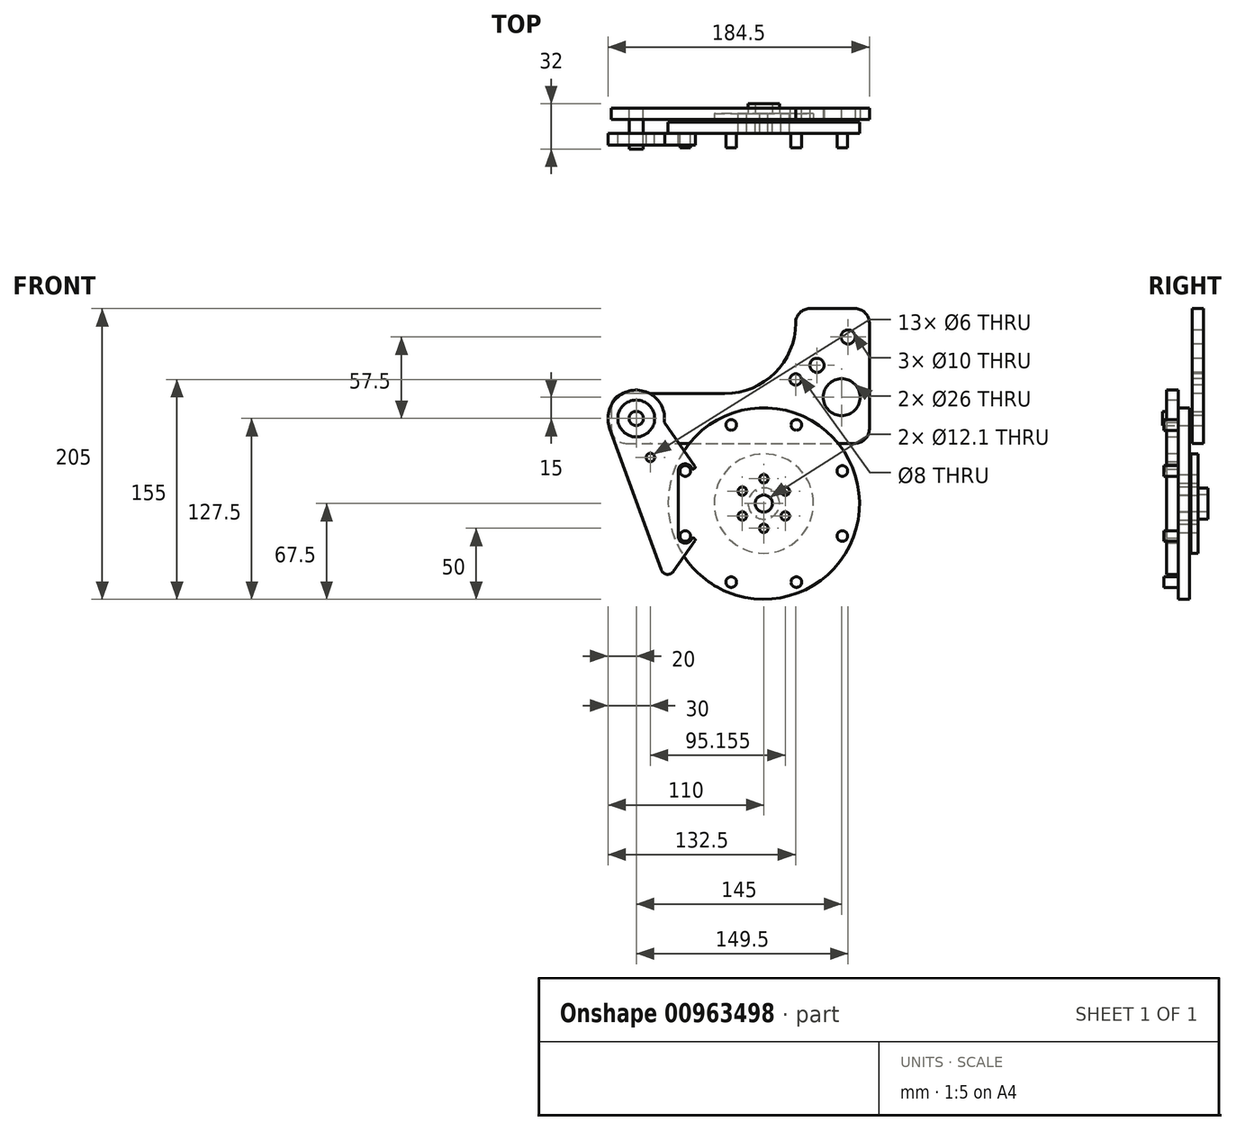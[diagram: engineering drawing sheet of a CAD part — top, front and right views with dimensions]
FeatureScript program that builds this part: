
annotation { "Feature Type Name" : "Feature", "Feature Type Description" : "" }
export const myFeature = defineFeature(function(context is Context, id is Id, definition is map)
    precondition{}
    {
        {
            var Q0;
            Q0=qCreatedBy(makeId("Front.planeOp"),FACE);
            var sketch = newSketch(context, id + "F0", { "sketchPlane" : qUnion([Q0])});
            skCircle(sketch, "E0", {"center": v(0, 0) * mm, "radius": 67.5 * mm});
            skCircle(sketch, "E1", {"center": v(0, 0) * mm, "radius": 6.05 * mm});
            skSolve(sketch);
        }
        {
            var Q0;
            Q0=qSketchRegion(id+"F0",true);
            extrude(context, id + "F1", {"entities" : qUnion([Q0]), "depth" : 5 * mm, "hasSecondDirection" : true, "secondDirectionOppositeDirection" : true, "secondDirectionDepth" : 3 * mm});
        }
        {
            var Q0;
            Q0=makeQuery(id+"F1.opExtrude","CAP_FACE",FACE,{"disambiguationData":[OSD([sQuery(id+"F0.wireOp",EDGE,"E0"),sQuery(id+"F0.wireOp",EDGE,"E1")])],"isStart":false});
            var sketch = newSketch(context, id + "F2", { "sketchPlane" : qUnion([Q0])});
            skCircle(sketch, "E2", {"center": v(0, 0) * mm, "radius": 60 * mm, "construction": true});
            skCircle(sketch, "E3", {"center": v(0, 60) * mm, "radius": 3.75 * mm});
            skCircle(sketch, "E4.1.0", {"center": v(-42.43, 42.43) * mm, "radius": 3.75 * mm});
            skCircle(sketch, "E4.2.0", {"center": v(-60, 0) * mm, "radius": 3.75 * mm});
            skCircle(sketch, "E4.3.0", {"center": v(-42.43, -42.43) * mm, "radius": 3.75 * mm});
            skCircle(sketch, "E4.4.0", {"center": v(0, -60) * mm, "radius": 3.75 * mm});
            skCircle(sketch, "E4.5.0", {"center": v(42.43, -42.43) * mm, "radius": 3.75 * mm});
            skCircle(sketch, "E4.6.0", {"center": v(60, 0) * mm, "radius": 3.75 * mm});
            skCircle(sketch, "E4.7.0", {"center": v(42.43, 42.43) * mm, "radius": 3.75 * mm});
            skPoint(sketch, "E5", {"position": v(0, -77) * mm});
            skSolve(sketch);
        }
        {
            var Q0;
            Q0=qSketchRegion(id+"F2",true);
            extrude(context, id + "F3", {"entities" : qUnion([Q0]), "operationType" : NewBodyOperationType.ADD, "depth" : 10 * mm});
        }
        {
            var Q0;
            Q0=qCreatedBy(makeId("Right.planeOp"),FACE);
            var sketch = newSketch(context, id + "F4", { "sketchPlane" : qUnion([Q0])});
            skLineSegment(sketch, "E6", {"start": v(-64.67, -77) * mm, "end": v(70.6, -77) * mm});
            skLineSegment(sketch, "E7", {"start": v(-72, 0) * mm, "end": v(117.3, 0) * mm});
            skLineSegment(sketch, "E8", {"start": v(-81.45, 67) * mm, "end": v(84.45, 67) * mm});
            skSolve(sketch);
        }
        {
            var Q0;
            Q0=makeQuery(id+"F1.opExtrude","CAP_FACE",FACE,{"disambiguationData":[OSD([sQuery(id+"F0.wireOp",EDGE,"E0"),sQuery(id+"F0.wireOp",EDGE,"E1")])],"isStart":false});
            var sketch = newSketch(context, id + "F5", { "sketchPlane" : qUnion([Q0])});
            skLineSegment(sketch, "E9", {"start": v(22.5, 127.5) * mm, "end": v(22.5, 127.5) * mm});
            skLineSegment(sketch, "E10", {"start": v(-27.5, 77.5) * mm, "end": v(-97.5, 77.5) * mm});
            skLineSegment(sketch, "E11", {"start": v(-107.5, 67.5) * mm, "end": v(-107.5, 52.5) * mm});
            skLineSegment(sketch, "E12", {"start": v(-97.5, 42.5) * mm, "end": v(-75.62, 42.5) * mm});
            skLineSegment(sketch, "E13", {"start": v(64.5, 137.5) * mm, "end": v(32.5, 137.5) * mm});
            skCircle(sketch, "E14", {"center": v(55, 75) * mm, "radius": 13 * mm});
            skCircle(sketch, "E15", {"center": v(-90, 60) * mm, "radius": 5 * mm});
            skCircle(sketch, "E16", {"center": v(59.5, 117.5) * mm, "radius": 5 * mm});
            skCircle(sketch, "E17", {"center": v(37.5, 97.5) * mm, "radius": 5 * mm});
            skPoint(sketch, "E18.visualSharp", {"position": v(-107.5, 77.5) * mm});
            skArc(sketch, "E18.filletArc", {"start": v(-97.5, 77.5) * mm, "mid": v(-104.57, 74.57) * mm, "end": v(-107.5, 67.5) * mm});
            skPoint(sketch, "E19.visualSharp", {"position": v(-107.5, 42.5) * mm});
            skArc(sketch, "E19.filletArc", {"start": v(-107.5, 52.5) * mm, "mid": v(-104.57, 45.43) * mm, "end": v(-97.5, 42.5) * mm});
            skArc(sketch, "E20.filletArc", {"start": v(-27.5, 77.5) * mm, "mid": v(7.86, 92.14) * mm, "end": v(22.5, 127.5) * mm});
            skArc(sketch, "E21.filletArc", {"start": v(32.5, 137.5) * mm, "mid": v(25.43, 134.57) * mm, "end": v(22.5, 127.5) * mm});
            skLineSegment(sketch, "E22", {"start": v(74.5, 127.5) * mm, "end": v(74.5, 52.5) * mm});
            skPoint(sketch, "E23.visualSharp", {"position": v(74.5, 137.5) * mm});
            skArc(sketch, "E23.filletArc", {"start": v(74.5, 127.5) * mm, "mid": v(71.57, 134.57) * mm, "end": v(64.5, 137.5) * mm});
            skPoint(sketch, "E24.visualSharp", {"position": v(74.5, 42.5) * mm});
            skArc(sketch, "E24.filletArc", {"start": v(64.5, 42.5) * mm, "mid": v(71.57, 45.43) * mm, "end": v(74.5, 52.5) * mm});
            skLineSegment(sketch, "E25.trimOffspring", {"start": v(-75.62, 42.5) * mm, "end": v(64.5, 42.5) * mm});
            skCircle(sketch, "E26", {"center": v(22.5, 87.5) * mm, "radius": 4 * mm});
            skSolve(sketch);
        }
        {
            var Q0;
            Q0=makeQuery(id+"F1.opExtrude","SWEPT_BODY",BODY,{"disambiguationData":[OSD([sQuery(id+"F0.wireOp",EDGE,"E0"),sQuery(id+"F0.wireOp",EDGE,"E1")])]});
            var Q1;
            Q1=sQuery(id+"F4.wireOp",EDGE,"E7");
            transform(context, id + "F6", {"entities" : qUnion([Q0]), "transformType" : TransformType.ROTATION, "transformAxis" : qUnion([Q1]), "angle" : 22.5 * degree, "makeCopy" : false});
        }
        {
            var Q0;
            Q0=qSketchRegion(id+"F5",true);
            extrude(context, id + "F7", {"entities" : qUnion([Q0]), "oppositeDirection" : true, "depth" : 8 * mm});
        }
        {
            var Q0;
            Q0=makeQuery(id+"F7.opExtrude","SWEPT_BODY",BODY,{"disambiguationData":[OSD([sQuery(id+"F5.wireOp",EDGE,"E9"),sQuery(id+"F5.wireOp",EDGE,"E10"),sQuery(id+"F5.wireOp",EDGE,"E11"),sQuery(id+"F5.wireOp",EDGE,"E12"),sQuery(id+"F5.wireOp",EDGE,"E13"),sQuery(id+"F5.wireOp",EDGE,"E14"),sQuery(id+"F5.wireOp",EDGE,"E15"),sQuery(id+"F5.wireOp",EDGE,"E16"),sQuery(id+"F5.wireOp",EDGE,"E17"),sQuery(id+"F5.wireOp",EDGE,"E18.filletArc"),sQuery(id+"F5.wireOp",EDGE,"E19.filletArc"),sQuery(id+"F5.wireOp",EDGE,"E20.filletArc"),sQuery(id+"F5.wireOp",EDGE,"E21.filletArc"),sQuery(id+"F5.wireOp",EDGE,"E22"),sQuery(id+"F5.wireOp",EDGE,"E23.filletArc"),sQuery(id+"F5.wireOp",EDGE,"E24.filletArc"),sQuery(id+"F5.wireOp",EDGE,"E25.trimOffspring")])]});
            transform(context, id + "F8", {"entities" : qUnion([Q0]), "transformType" : TransformType.TRANSLATION_3D, "dx" : 0 * mm, "dy" : 10 * mm, "dz" : 0 * mm, "makeCopy" : false});
        }
        {
            var Q0;
            Q0=makeQuery(id+"F1.opExtrude","CAP_FACE",FACE,{"disambiguationData":[OSD([sQuery(id+"F0.wireOp",EDGE,"E0"),sQuery(id+"F0.wireOp",EDGE,"E1")])],"isStart":false});
            var sketch = newSketch(context, id + "F9", { "sketchPlane" : qUnion([Q0])});
            skCircle(sketch, "E27", {"center": v(-90, 60) * mm, "radius": 13 * mm});
            skArc(sketch, "E28", {"start": v(-70.2, 57.14) * mm, "mid": v(-92.05, 79.9) * mm, "end": v(-108.8, 53.16) * mm});
            skLineSegment(sketch, "E29", {"start": v(-48.55, -26.21) * mm, "end": v(-63.67, -47.8) * mm});
            skLineSegment(sketch, "E30", {"start": v(-72.47, -46.65) * mm, "end": v(-108.8, 53.16) * mm});
            skPoint(sketch, "E31.visualSharp", {"position": v(-69.18, -55.67) * mm});
            skArc(sketch, "E31.filletArc", {"start": v(-72.47, -46.65) * mm, "mid": v(-68.42, -49.9) * mm, "end": v(-63.67, -47.8) * mm});
            skCircle(sketch, "E32", {"center": v(-80, 32.5) * mm, "radius": 3 * mm});
            skArc(sketch, "E33", {"start": v(-60.43, -22.96) * mm, "mid": v(-56.44, -27.86) * mm, "end": v(-50.84, -24.93) * mm});
            skLineSegment(sketch, "E34", {"start": v(-48.87, -24.77) * mm, "end": v(-49.42, -24.46) * mm});
            skPoint(sketch, "E35.visualSharp", {"position": v(-47.93, -25.32) * mm});
            skArc(sketch, "E35.filletArc", {"start": v(-48.55, -26.21) * mm, "mid": v(-48.4, -25.42) * mm, "end": v(-48.87, -24.77) * mm});
            skArc(sketch, "E36", {"start": v(-50.84, 24.93) * mm, "mid": v(-56.44, 27.86) * mm, "end": v(-60.43, 22.96) * mm});
            skLineSegment(sketch, "E37", {"start": v(-60.43, 22.96) * mm, "end": v(-60.43, -22.96) * mm});
            skLineSegment(sketch, "E38", {"start": v(-70.2, 57.14) * mm, "end": v(-48.55, 26.21) * mm});
            skLineSegment(sketch, "E39", {"start": v(-55.43, -22.96) * mm, "end": v(-50.5, -23.83) * mm, "construction": true});
            skPoint(sketch, "E40.visualSharp", {"position": v(-50.5, -23.83) * mm});
            skArc(sketch, "E40.filletArc", {"start": v(-49.42, -24.46) * mm, "mid": v(-50.23, -24.38) * mm, "end": v(-50.84, -24.93) * mm});
            skLineSegment(sketch, "E41", {"start": v(-55.43, 22.96) * mm, "end": v(-50.5, 23.83) * mm, "construction": true});
            skLineSegment(sketch, "E42", {"start": v(-48.87, 24.77) * mm, "end": v(-49.42, 24.46) * mm});
            skPoint(sketch, "E43.visualSharp", {"position": v(-50.5, 23.83) * mm});
            skArc(sketch, "E43.filletArc", {"start": v(-50.84, 24.93) * mm, "mid": v(-50.23, 24.38) * mm, "end": v(-49.42, 24.46) * mm});
            skPoint(sketch, "E44.visualSharp", {"position": v(-47.93, 25.32) * mm});
            skArc(sketch, "E44.filletArc", {"start": v(-48.87, 24.77) * mm, "mid": v(-48.4, 25.42) * mm, "end": v(-48.55, 26.21) * mm});
            skSolve(sketch);
        }
        {
            var Q0;
            Q0=qSketchRegion(id+"F9",true);
            extrude(context, id + "F10", {"entities" : qUnion([Q0]), "depth" : 8 * mm});
        }
        {
            var Q0;
            Q0=qCreatedBy(makeId("Top.planeOp"),FACE);
            var sketch = newSketch(context, id + "F11", { "sketchPlane" : qUnion([Q0])});
            skLineSegment(sketch, "E45", {"start": v(-6.05, 4) * mm, "end": v(-6.05, 16) * mm});
            skLineSegment(sketch, "E46", {"start": v(-6.05, 16) * mm, "end": v(-11.05, 16) * mm});
            skLineSegment(sketch, "E47", {"start": v(-11.05, 16) * mm, "end": v(-11.05, 9) * mm});
            skLineSegment(sketch, "E48", {"start": v(-11.05, 9) * mm, "end": v(-35, 9) * mm});
            skLineSegment(sketch, "E49", {"start": v(-35, 9) * mm, "end": v(-35, 4) * mm});
            skLineSegment(sketch, "E50", {"start": v(-35, 4) * mm, "end": v(-6.05, 4) * mm});
            skLineSegment(sketch, "E51", {"start": v(0, -36.2) * mm, "end": v(0, 47.53) * mm, "construction": true});
            skSolve(sketch);
        }
        {
            var Q0;
            Q0=qSketchRegion(id+"F11",true);
            var Q1;
            Q1=sQuery(id+"F11.wireOp",EDGE,"E51");
            revolve(context, id + "F12", {"entities" : qUnion([Q0]), "axis" : qUnion([Q1]), "revolveType" : RevolveType.FULL});
        }
        {
            var Q0;
            Q0=makeQuery(id+"F12.opRevolve","SWEPT_FACE",FACE,{"disambiguationData":[OSD([sQuery(id+"F11.wireOp",EDGE,"E48")])]});
            var sketch = newSketch(context, id + "F13", { "sketchPlane" : qUnion([Q0])});
            skCircle(sketch, "E52", {"center": v(0, 17.5) * mm, "radius": 3 * mm});
            skCircle(sketch, "E53.1.0", {"center": v(-15.16, 8.75) * mm, "radius": 3 * mm});
            skCircle(sketch, "E53.2.0", {"center": v(-15.16, -8.75) * mm, "radius": 3 * mm});
            skCircle(sketch, "E53.3.0", {"center": v(0, -17.5) * mm, "radius": 3 * mm});
            skCircle(sketch, "E53.4.0", {"center": v(15.16, -8.75) * mm, "radius": 3 * mm});
            skPoint(sketch, "E53.center", {"position": v(0, 0) * mm});
            skCircle(sketch, "E54.1.5.0", {"center": v(15.16, 8.75) * mm, "radius": 3 * mm});
            skSolve(sketch);
        }
        {
            var Q0;
            Q0=qSketchRegion(id+"F13",true);
            extrude(context, id + "F14", {"entities" : qUnion([Q0]), "operationType" : NewBodyOperationType.REMOVE, "oppositeDirection" : true, "depth" : 25 * mm});
        }
        {
            var Q0;
            Q0=makeQuery(id+"F7.opExtrude","CAP_FACE",FACE,{"disambiguationData":[OSD([sQuery(id+"F5.wireOp",EDGE,"E9"),sQuery(id+"F5.wireOp",EDGE,"E10"),sQuery(id+"F5.wireOp",EDGE,"E11"),sQuery(id+"F5.wireOp",EDGE,"E12"),sQuery(id+"F5.wireOp",EDGE,"E13"),sQuery(id+"F5.wireOp",EDGE,"E14"),sQuery(id+"F5.wireOp",EDGE,"E15"),sQuery(id+"F5.wireOp",EDGE,"E16"),sQuery(id+"F5.wireOp",EDGE,"E17"),sQuery(id+"F5.wireOp",EDGE,"E18.filletArc"),sQuery(id+"F5.wireOp",EDGE,"E19.filletArc"),sQuery(id+"F5.wireOp",EDGE,"E20.filletArc"),sQuery(id+"F5.wireOp",EDGE,"E21.filletArc"),sQuery(id+"F5.wireOp",EDGE,"E22"),sQuery(id+"F5.wireOp",EDGE,"E23.filletArc"),sQuery(id+"F5.wireOp",EDGE,"E24.filletArc"),sQuery(id+"F5.wireOp",EDGE,"E25.trimOffspring")])],"isStart":false});
            var sketch = newSketch(context, id + "F15", { "sketchPlane" : qUnion([Q0])});
            skCircle(sketch, "E55", {"center": v(90, 60) * mm, "radius": 5 * mm});
            skSolve(sketch);
        }
        {
            var Q0;
            Q0=qSketchRegion(id+"F15",true);
            extrude(context, id + "F16", {"entities" : qUnion([Q0]), "oppositeDirection" : true, "depth" : 29 * mm});
        }
    });
